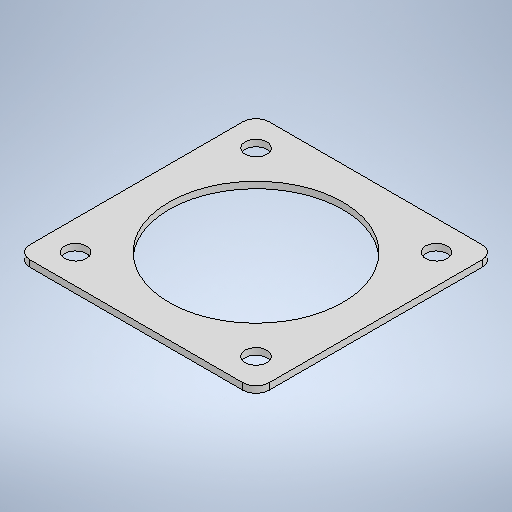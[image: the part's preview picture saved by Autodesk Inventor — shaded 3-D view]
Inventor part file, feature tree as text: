
AUTODESK INVENTOR PART (.ipt)
format: ipt  version: 2025.1 (Build 291241020, 241B)  size: 366,592 bytes
history: native  units: mm
features: sketch x6, sheet_metal_op x4, extrude x3, other x3, pattern_linear x2, chamfer x1, projected_geometry x1
ambient origin geometry x8: Origin, YZ Plane, XZ Plane, XY Plane, X Axis, Y Axis, Z Axis, Center Point
bodies: Solid1 (feature_tree)
feature tree (20):
  sheet_metal_op  "Face1"
  sheet_metal_op  "Flange2"
  extrude  "Extrusion2"  Depth=3.0mm
  pattern_linear  "Rectangular Pattern1"  Count1=20  [1 undecoded]
  extrude  "Extrusion3"  Depth=3.0mm
  pattern_linear  "Rectangular Pattern2"  Count1=5 Spacing1=90.0deg
  extrude  "Extrusion4"  Depth=5.0mm
  chamfer  "Corner Round1"
  sketch  "Sketch1"  dims[d2=3.0mm d25=400.0mm d26=200.0mm]
  other  "Plate1"
  sketch  "Sketch5"  dims[d27=3.0mm d28=1.5mm]
  other  "Plate3"
  sheet_metal_op  "Bend2"
  sheet_metal_op  "Corner2"
  sketch  "Sketch6"  dims[d29=6.0mm]
  sketch  "Sketch7"  dims[d30=5.0mm d31=50.0mm d32=90.0deg d33=5.0mm]
  projected_geometry  "Projected Loop2"
  sketch  "Sketch8"  dims[d34=12.0mm d35=1.0mm d36=5.0mm]
  sketch  "Sketch9"  dims[d37=32.0mm d38=150.0mm d39=3.0mm d40=0.0mm d41=13.0mm d42=25.0mm d43=0.0mm d44=0.0mm d45=30.0mm d47=162.0mm d48=13.0mm d49=25.0mm d50=0.0mm d51=0.0mm d52=30.0mm d54=72.0mm d55=10.0mm d56=83.0mm d57=83.0mm d58=110.0mm d59=110.0mm d60=80.0mm d61=0.0mm d62=0.0mm d63=6.0mm]
  other  "Cut1"
note: 1 required parameter value undecoded (feature->parameter linkage not recoverable at this tier; creation-order binding heuristic only, values carry confidence <= 0.55)
